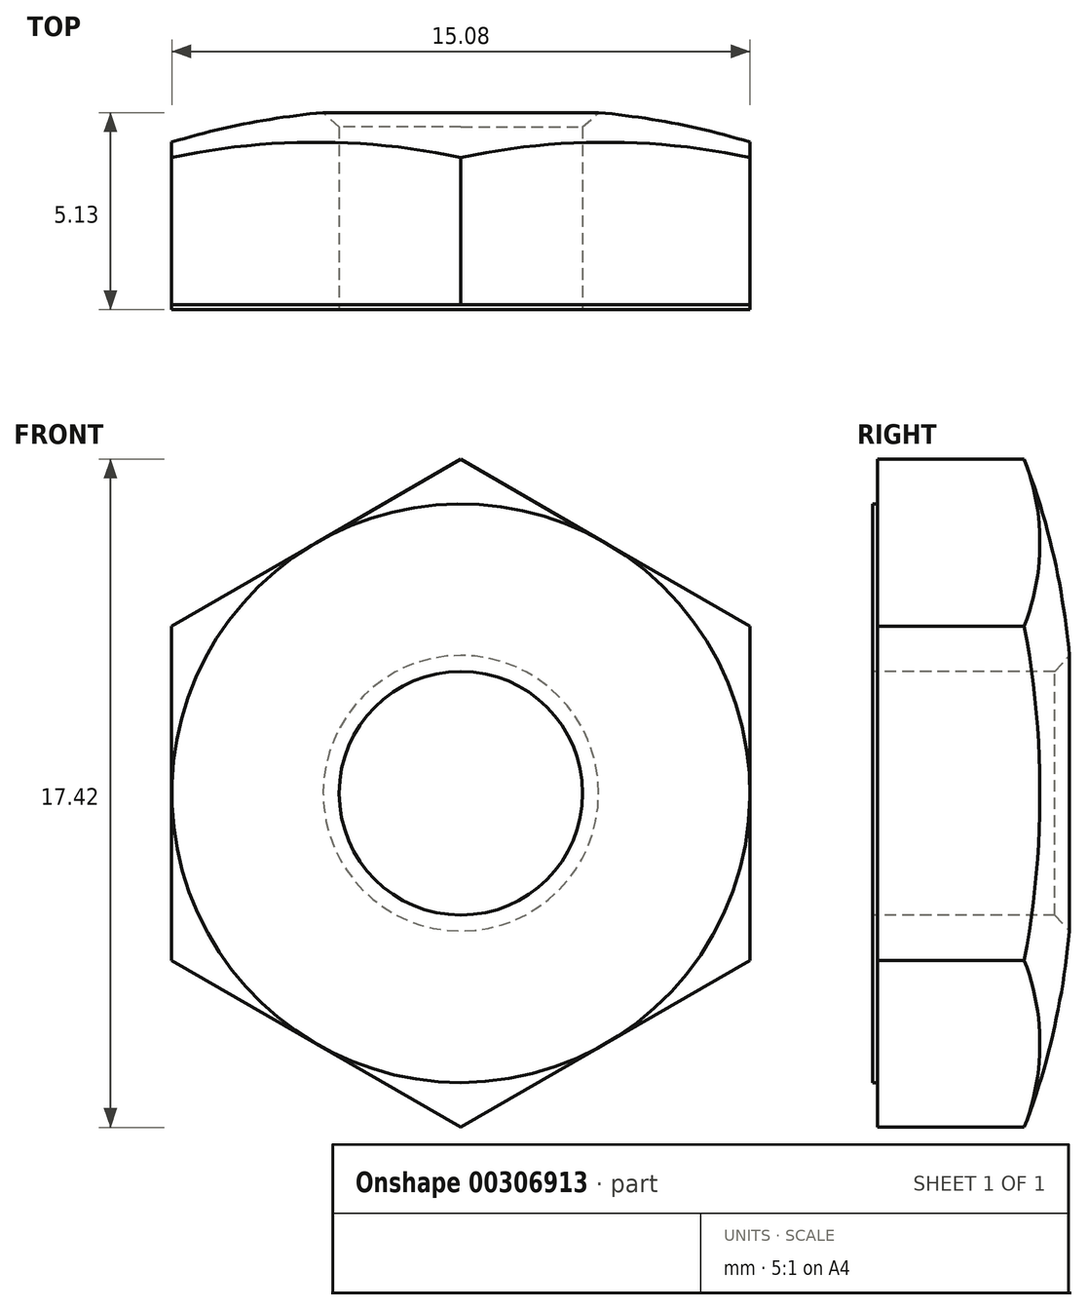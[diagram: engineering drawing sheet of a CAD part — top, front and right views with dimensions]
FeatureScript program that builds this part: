
annotation { "Feature Type Name" : "Feature", "Feature Type Description" : "" }
export const myFeature = defineFeature(function(context is Context, id is Id, definition is map)
    precondition{}
    {
        {
            var Q0;
            Q0=qCreatedBy(makeId("Front.planeOp"),FACE);
            var sketch = newSketch(context, id + "F0", { "sketchPlane" : qUnion([Q0])});
            skCircle(sketch, "E0.cCircle", {"center": v(0, 0) * mm, "radius": 7.54 * mm});
            skLineSegment(sketch, "E0.0", {"start": v(7.54, 4.35) * mm, "end": v(7.54, -4.35) * mm});
            skLineSegment(sketch, "E0.1", {"start": v(7.54, -4.35) * mm, "end": v(0, -8.7) * mm});
            skLineSegment(sketch, "E0.2", {"start": v(0, -8.7) * mm, "end": v(-7.54, -4.35) * mm});
            skLineSegment(sketch, "E0.3", {"start": v(-7.54, -4.35) * mm, "end": v(-7.54, 4.35) * mm});
            skLineSegment(sketch, "E0.4", {"start": v(-7.54, 4.35) * mm, "end": v(0, 8.7) * mm});
            skLineSegment(sketch, "E0.5", {"start": v(0, 8.7) * mm, "end": v(7.54, 4.35) * mm});
            skPoint(sketch, "E0.0.midPoint", {"position": v(7.54, 0) * mm});
            skCircle(sketch, "E1", {"center": v(0, 0) * mm, "radius": 3.18 * mm});
            skSolve(sketch);
        }
        {
            var Q0;
            Q0=makeQuery(id+"F0.imprint","IMPRINT",FACE,{"disambiguationData":[TD([[makeQuery(id+"F0.imprint","IMPRINT",EDGE,{"derivedFrom":sQuery(id+"F0.wireOp",EDGE,"E1")}),-1.0]])]});
            var Q1;
            {var subQ0=sQuery(id+"F0.wireOp",EDGE,"E0.5");var subQ1=sQuery(id+"F0.wireOp",EDGE,"E0.cCircle");var subQ2=makeQuery(id+"F0.imprint","INTERSECT",VERTEX,{"derivedFrom":[subQ1,subQ0]});Q1=makeQuery(id+"F0.imprint","IMPRINT",FACE,{"disambiguationData":[TD([[makeQuery(id+"F0.imprint","IMPRINT",EDGE,{"disambiguationData":[TD([[subQ2,-1.0]])],"derivedFrom":subQ1}),-1.0]])]});}
            var Q2;
            {var subQ0=sQuery(id+"F0.wireOp",EDGE,"E0.5");var subQ1=sQuery(id+"F0.wireOp",EDGE,"E0.cCircle");var subQ2=makeQuery(id+"F0.imprint","INTERSECT",VERTEX,{"derivedFrom":[subQ1,subQ0]});Q2=makeQuery(id+"F0.imprint","IMPRINT",FACE,{"disambiguationData":[TD([[makeQuery(id+"F0.imprint","IMPRINT",EDGE,{"disambiguationData":[TD([[subQ2,1.0]])],"derivedFrom":subQ1}),-1.0]])]});}
            var Q3;
            {var subQ0=sQuery(id+"F0.wireOp",EDGE,"E0.0");var subQ1=sQuery(id+"F0.wireOp",EDGE,"E0.cCircle");var subQ2=makeQuery(id+"F0.imprint","INTERSECT",VERTEX,{"derivedFrom":[subQ1,subQ0]});Q3=makeQuery(id+"F0.imprint","IMPRINT",FACE,{"disambiguationData":[TD([[makeQuery(id+"F0.imprint","IMPRINT",EDGE,{"disambiguationData":[TD([[subQ2,1.0]])],"derivedFrom":subQ1}),-1.0]])]});}
            var Q4;
            {var subQ0=sQuery(id+"F0.wireOp",EDGE,"E0.2");var subQ1=sQuery(id+"F0.wireOp",EDGE,"E0.cCircle");var subQ2=makeQuery(id+"F0.imprint","INTERSECT",VERTEX,{"derivedFrom":[subQ1,subQ0]});Q4=makeQuery(id+"F0.imprint","IMPRINT",FACE,{"disambiguationData":[TD([[makeQuery(id+"F0.imprint","IMPRINT",EDGE,{"disambiguationData":[TD([[subQ2,-1.0]])],"derivedFrom":subQ1}),-1.0]])]});}
            var Q5;
            {var subQ0=sQuery(id+"F0.wireOp",EDGE,"E0.3");var subQ1=sQuery(id+"F0.wireOp",EDGE,"E0.cCircle");var subQ2=makeQuery(id+"F0.imprint","INTERSECT",VERTEX,{"derivedFrom":[subQ1,subQ0]});Q5=makeQuery(id+"F0.imprint","IMPRINT",FACE,{"disambiguationData":[TD([[makeQuery(id+"F0.imprint","IMPRINT",EDGE,{"disambiguationData":[TD([[subQ2,-1.0]])],"derivedFrom":subQ1}),-1.0]])]});}
            var Q6;
            {var subQ0=sQuery(id+"F0.wireOp",EDGE,"E0.4");var subQ1=sQuery(id+"F0.wireOp",EDGE,"E0.cCircle");var subQ2=makeQuery(id+"F0.imprint","INTERSECT",VERTEX,{"derivedFrom":[subQ1,subQ0]});Q6=makeQuery(id+"F0.imprint","IMPRINT",FACE,{"disambiguationData":[TD([[makeQuery(id+"F0.imprint","IMPRINT",EDGE,{"disambiguationData":[TD([[subQ2,-1.0]])],"derivedFrom":subQ1}),-1.0]])]});}
            extrude(context, id + "F1", {"entities" : qUnion([Q0, Q1, Q2, Q3, Q4, Q5, Q6]), "oppositeDirection" : true, "depth" : 5.08 * mm});
        }
        {
            var Q0;
            Q0=qCreatedBy(makeId("Right.planeOp"),FACE);
            var sketch = newSketch(context, id + "F2", { "sketchPlane" : qUnion([Q0])});
            skLineSegment(sketch, "E2", {"start": v(0, 0) * mm, "end": v(7.73, 0) * mm, "construction": true});
            skLineSegment(sketch, "E3", {"start": v(0, 8.74) * mm, "end": v(3.81, 8.74) * mm, "construction": true});
            skLineSegment(sketch, "E4", {"start": v(3.81, 8.74) * mm, "end": v(3.81, 10.34) * mm, "construction": true});
            skFitSpline(sketch, "E5", {"points": [v(3.81, 8.74) * mm, v(5.1, 0) * mm], "startDerivative": vector(4.54, -11.54) * mm, "endDerivative": vector(0, -3.68) * mm});
            skLineSegment(sketch, "E6", {"start": v(3.81, 8.74) * mm, "end": v(3.81, 9.1) * mm});
            skLineSegment(sketch, "E7", {"start": v(3.81, 9.1) * mm, "end": v(5.84, 9.1) * mm});
            skLineSegment(sketch, "E8", {"start": v(5.84, 9.1) * mm, "end": v(5.71, 0) * mm});
            skLineSegment(sketch, "E9", {"start": v(5.71, 0) * mm, "end": v(5.1, 0) * mm});
            skSolve(sketch);
        }
        {
            var Q0;
            Q0=makeQuery(id+"F2.imprint","IMPRINT",FACE,{"disambiguationData":[TD([[makeQuery(id+"F2.imprint","IMPRINT",EDGE,{"derivedFrom":sQuery(id+"F2.wireOp",EDGE,"E5")}),1.0]])]});
            var Q1;
            Q1=sQuery(id+"F2.wireOp",EDGE,"E2");
            revolve(context, id + "F3", {"operationType" : NewBodyOperationType.REMOVE, "entities" : qUnion([Q0]), "axis" : qUnion([Q1]), "revolveType" : RevolveType.FULL, "oppositeDirection" : true});
        }
        {
            var Q0;
            Q0=makeQuery(id+"F0.imprint","IMPRINT",FACE,{"disambiguationData":[TD([[makeQuery(id+"F0.imprint","IMPRINT",EDGE,{"derivedFrom":sQuery(id+"F0.wireOp",EDGE,"E1")}),-1.0]])]});
            extrude(context, id + "F4", {"entities" : qUnion([Q0]), "operationType" : NewBodyOperationType.ADD, "depth" : 0.13 * mm});
        }
        {
            var Q0;
            Q0=makeQuery(id+"F3.boolean.opBoolean","INTERSECT",EDGE,{"derivedFrom":[makeQuery(id+"F1.opExtrude","SWEPT_FACE",FACE,{"disambiguationData":[OSD([sQuery(id+"F0.wireOp",EDGE,"E1")])]}),makeQuery(id+"F3.opRevolve","SWEPT_FACE",FACE,{"disambiguationData":[OSD([sQuery(id+"F2.wireOp",EDGE,"E5")])]})]});
            chamfer(context, id + "F5", {"entities" : qUnion([Q0]), "width" : 0.38 * mm, "tangentPropagation" : true});
        }
    });
